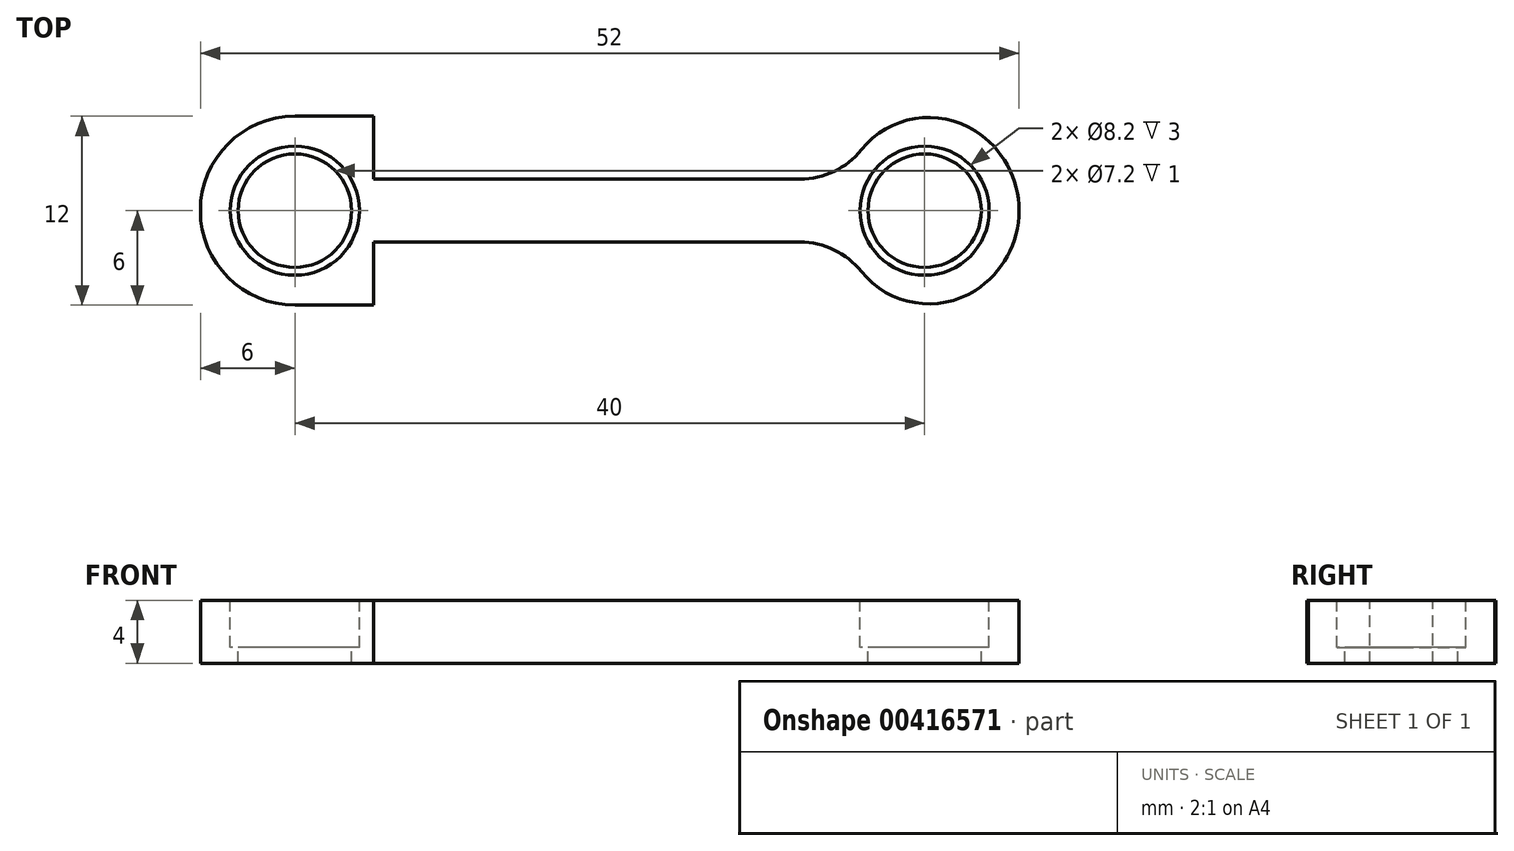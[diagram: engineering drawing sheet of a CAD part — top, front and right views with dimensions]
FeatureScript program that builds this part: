
annotation { "Feature Type Name" : "Feature", "Feature Type Description" : "" }
export const myFeature = defineFeature(function(context is Context, id is Id, definition is map)
    precondition{}
    {
        {
            var Q0;
            Q0=qCreatedBy(makeId("Top.planeOp"),FACE);
            var sketch = newSketch(context, id + "F0", { "sketchPlane" : qUnion([Q0])});
            skLineSegment(sketch, "E0.bottom", {"start": v(-19.88, 0) * mm, "end": v(32.12, 0) * mm});
            skLineSegment(sketch, "E0.top", {"start": v(-19.88, 12) * mm, "end": v(32.12, 12) * mm});
            skLineSegment(sketch, "E0.left", {"start": v(-19.88, 0) * mm, "end": v(-19.88, 12) * mm});
            skLineSegment(sketch, "E0.right", {"start": v(32.12, 0) * mm, "end": v(32.12, 12) * mm});
            skSolve(sketch);
        }
        {
            var Q0;
            Q0=makeQuery(id+"F0.imprint","IMPRINT",FACE,{"disambiguationData":[TD([[makeQuery(id+"F0.imprint","IMPRINT",EDGE,{"derivedFrom":sQuery(id+"F0.wireOp",EDGE,"E0.bottom")}),1.0]])]});
            extrude(context, id + "F1", {"entities" : qUnion([Q0]), "depth" : 4 * mm});
        }
        {
            var Q0;
            Q0=makeQuery(id+"F1.opExtrude","CAP_FACE",FACE,{"disambiguationData":[OSD([sQuery(id+"F0.wireOp",EDGE,"E0.bottom"),sQuery(id+"F0.wireOp",EDGE,"E0.top"),sQuery(id+"F0.wireOp",EDGE,"E0.left"),sQuery(id+"F0.wireOp",EDGE,"E0.right")])],"isStart":false});
            var sketch = newSketch(context, id + "F2", { "sketchPlane" : qUnion([Q0])});
            skCircle(sketch, "E1", {"center": v(26.12, 6) * mm, "radius": 4.1 * mm});
            skCircle(sketch, "E2", {"center": v(-13.88, 6) * mm, "radius": 4.1 * mm});
            skCircle(sketch, "E3", {"center": v(26.12, 6) * mm, "radius": 3.6 * mm});
            skCircle(sketch, "E4", {"center": v(-13.88, 6) * mm, "radius": 3.6 * mm});
            skSolve(sketch);
        }
        {
            var Q0;
            Q0=makeQuery(id+"F2.imprint","IMPRINT",FACE,{"disambiguationData":[TD([[makeQuery(id+"F2.imprint","IMPRINT",EDGE,{"derivedFrom":sQuery(id+"F2.wireOp",EDGE,"E2")}),1.0]])]});
            var Q1;
            Q1=makeQuery(id+"F2.imprint","IMPRINT",FACE,{"disambiguationData":[TD([[makeQuery(id+"F2.imprint","IMPRINT",EDGE,{"derivedFrom":sQuery(id+"F2.wireOp",EDGE,"KRTfRChP-nXbi-TgXD-2Nc6-GMDFCuTp6KQj")}),1.0]])]});
            var Q2;
            Q2=makeQuery(id+"F2.imprint","IMPRINT",FACE,{"disambiguationData":[TD([[makeQuery(id+"F2.imprint","IMPRINT",EDGE,{"derivedFrom":sQuery(id+"F2.wireOp",EDGE,"E1")}),1.0]])]});
            extrude(context, id + "F3", {"entities" : qUnion([Q0, Q1, Q2]), "operationType" : NewBodyOperationType.REMOVE, "oppositeDirection" : true, "depth" : 3 * mm});
        }
        {
            var Q0;
            Q0=makeQuery(id+"F2.imprint","IMPRINT",FACE,{"disambiguationData":[TD([[makeQuery(id+"F2.imprint","IMPRINT",EDGE,{"derivedFrom":sQuery(id+"F2.wireOp",EDGE,"E4")}),1.0]])]});
            var Q1;
            Q1=makeQuery(id+"F2.imprint","IMPRINT",FACE,{"disambiguationData":[TD([[makeQuery(id+"F2.imprint","IMPRINT",EDGE,{"derivedFrom":sQuery(id+"F2.wireOp",EDGE,"GlQmYsD8-ChJU-Foso-C0s5-5TPi7Piaeb3v")}),1.0]])]});
            var Q2;
            Q2=makeQuery(id+"F2.imprint","IMPRINT",FACE,{"disambiguationData":[TD([[makeQuery(id+"F2.imprint","IMPRINT",EDGE,{"derivedFrom":sQuery(id+"F2.wireOp",EDGE,"E3")}),1.0]])]});
            extrude(context, id + "F4", {"entities" : qUnion([Q0, Q1, Q2]), "operationType" : NewBodyOperationType.REMOVE, "oppositeDirection" : true, "depth" : 25 * mm});
        }
        {
            var Q0;
            Q0=makeQuery(id+"F1.opExtrude","SWEPT_EDGE",EDGE,{"disambiguationData":[OSD([sQuery(id+"F0.wireOp",EDGE,"E0.top"),sQuery(id+"F0.wireOp",EDGE,"E0.right")])]});
            var Q1;
            Q1=makeQuery(id+"F1.opExtrude","SWEPT_EDGE",EDGE,{"disambiguationData":[OSD([sQuery(id+"F0.wireOp",EDGE,"E0.bottom"),sQuery(id+"F0.wireOp",EDGE,"E0.right")])]});
            var Q2;
            Q2=makeQuery(id+"F1.opExtrude","SWEPT_EDGE",EDGE,{"disambiguationData":[OSD([sQuery(id+"F0.wireOp",EDGE,"E0.top"),sQuery(id+"F0.wireOp",EDGE,"E0.left")])]});
            var Q3;
            Q3=makeQuery(id+"F1.opExtrude","SWEPT_EDGE",EDGE,{"disambiguationData":[OSD([sQuery(id+"F0.wireOp",EDGE,"E0.bottom"),sQuery(id+"F0.wireOp",EDGE,"E0.left")])]});
            fillet(context, id + "F5", {"entities" : qUnion([Q0, Q1, Q2, Q3]), "radius" : 6 * mm, "tangentPropagation" : true, "allowEdgeOverflow" : false});
        }
        {
            var Q0;
            Q0=makeQuery(id+"F2.imprint","IMPRINT",FACE,{"disambiguationData":[TD([[makeQuery(id+"F2.imprint","IMPRINT",EDGE,{"derivedFrom":sQuery(id+"F2.wireOp",EDGE,"E1")}),-1.0]])]});
            var sketch = newSketch(context, id + "F6", { "sketchPlane" : qUnion([Q0])});
            skLineSegment(sketch, "E5.bottom", {"start": v(-8.88, 12) * mm, "end": v(21.12, 12) * mm});
            skLineSegment(sketch, "E5.top", {"start": v(-8.88, 8) * mm, "end": v(21.12, 8) * mm});
            skLineSegment(sketch, "E5.left", {"start": v(-8.88, 12) * mm, "end": v(-8.88, 8) * mm});
            skLineSegment(sketch, "E5.right", {"start": v(21.12, 12) * mm, "end": v(21.12, 8) * mm});
            skLineSegment(sketch, "E6.bottom", {"start": v(-8.88, 0) * mm, "end": v(21.12, 0) * mm});
            skLineSegment(sketch, "E6.top", {"start": v(-8.88, 4) * mm, "end": v(21.12, 4) * mm});
            skLineSegment(sketch, "E6.left", {"start": v(-8.88, 0) * mm, "end": v(-8.88, 4) * mm});
            skLineSegment(sketch, "E6.right", {"start": v(21.12, 0) * mm, "end": v(21.12, 4) * mm});
            skSolve(sketch);
        }
        {
            var Q0;
            Q0=makeQuery(id+"F6.imprint","IMPRINT",FACE,{"disambiguationData":[TD([[makeQuery(id+"F6.imprint","IMPRINT",EDGE,{"derivedFrom":sQuery(id+"F6.wireOp",EDGE,"E5.bottom")}),-1.0]])]});
            var Q1;
            Q1=makeQuery(id+"F6.imprint","IMPRINT",FACE,{"disambiguationData":[TD([[makeQuery(id+"F6.imprint","IMPRINT",EDGE,{"derivedFrom":sQuery(id+"F6.wireOp",EDGE,"E6.bottom")}),1.0]])]});
            extrude(context, id + "F7", {"entities" : qUnion([Q0, Q1]), "operationType" : NewBodyOperationType.REMOVE, "oppositeDirection" : true, "depth" : 25 * mm});
        }
        {
            var Q0;
            Q0=makeQuery(id+"F7.boolean.opBoolean","COPY",EDGE,{"derivedFrom":makeQuery(id+"F7.opExtrude","SWEPT_EDGE",EDGE,{"disambiguationData":[OSD([sQuery(id+"F0.wireOp",EDGE,"E0.top"),sQuery(id+"F6.wireOp",EDGE,"E5.bottom"),sQuery(id+"F6.wireOp",EDGE,"E5.left")])]})});
            var Q1;
            Q1=makeQuery(id+"F7.boolean.opBoolean","COPY",EDGE,{"derivedFrom":makeQuery(id+"F7.opExtrude","SWEPT_EDGE",EDGE,{"disambiguationData":[OSD([sQuery(id+"F0.wireOp",EDGE,"E0.bottom"),sQuery(id+"F6.wireOp",EDGE,"E6.bottom"),sQuery(id+"F6.wireOp",EDGE,"E6.left")])]})});
            var Q2;
            Q2=makeQuery(id+"F7.boolean.opBoolean","COPY",EDGE,{"derivedFrom":makeQuery(id+"F7.opExtrude","SWEPT_EDGE",EDGE,{"disambiguationData":[OSD([sQuery(id+"F0.wireOp",EDGE,"E0.bottom"),sQuery(id+"F6.wireOp",EDGE,"E6.bottom"),sQuery(id+"F6.wireOp",EDGE,"E6.right")])]})});
            var Q3;
            Q3=makeQuery(id+"F7.boolean.opBoolean","COPY",EDGE,{"derivedFrom":makeQuery(id+"F7.opExtrude","SWEPT_EDGE",EDGE,{"disambiguationData":[OSD([sQuery(id+"F0.wireOp",EDGE,"E0.top"),sQuery(id+"F6.wireOp",EDGE,"E5.bottom"),sQuery(id+"F6.wireOp",EDGE,"E5.right")])]})});
            fillet(context, id + "F8", {"entities" : qUnion([Q0, Q1, Q2, Q3]), "radius" : 5.5 * mm, "tangentPropagation" : true, "allowEdgeOverflow" : false});
        }
        {
            var Q0;
            Q0=makeQuery(id+"F8.opFillet","BLEND_EDGE",EDGE,{"blendedFrom":[makeQuery(id+"F7.boolean.opBoolean","COPY",EDGE,{"derivedFrom":makeQuery(id+"F7.opExtrude","SWEPT_EDGE",EDGE,{"disambiguationData":[OSD([sQuery(id+"F0.wireOp",EDGE,"E0.top"),sQuery(id+"F6.wireOp",EDGE,"E5.bottom"),sQuery(id+"F6.wireOp",EDGE,"E5.left")])]})}),makeQuery(id+"F7.boolean.opBoolean","COPY",FACE,{"derivedFrom":makeQuery(id+"F7.opExtrude","SWEPT_FACE",FACE,{"disambiguationData":[OSD([sQuery(id+"F6.wireOp",EDGE,"E5.top")])]})})],"blendedInto":[makeQuery(id+"F7.boolean.opBoolean","COPY",FACE,{"derivedFrom":makeQuery(id+"F7.opExtrude","SWEPT_FACE",FACE,{"disambiguationData":[OSD([sQuery(id+"F6.wireOp",EDGE,"E5.top")])]})})]});
            var Q1;
            Q1=makeQuery(id+"F8.opFillet","BLEND_EDGE",EDGE,{"blendedFrom":[makeQuery(id+"F7.boolean.opBoolean","COPY",EDGE,{"derivedFrom":makeQuery(id+"F7.opExtrude","SWEPT_EDGE",EDGE,{"disambiguationData":[OSD([sQuery(id+"F0.wireOp",EDGE,"E0.bottom"),sQuery(id+"F6.wireOp",EDGE,"E6.bottom"),sQuery(id+"F6.wireOp",EDGE,"E6.left")])]})}),makeQuery(id+"F7.boolean.opBoolean","COPY",FACE,{"derivedFrom":makeQuery(id+"F7.opExtrude","SWEPT_FACE",FACE,{"disambiguationData":[OSD([sQuery(id+"F6.wireOp",EDGE,"E6.top")])]})})],"blendedInto":[makeQuery(id+"F7.boolean.opBoolean","COPY",FACE,{"derivedFrom":makeQuery(id+"F7.opExtrude","SWEPT_FACE",FACE,{"disambiguationData":[OSD([sQuery(id+"F6.wireOp",EDGE,"E6.top")])]})})]});
            var Q2;
            Q2=makeQuery(id+"F8.opFillet","BLEND_EDGE",EDGE,{"blendedFrom":[makeQuery(id+"F7.boolean.opBoolean","COPY",EDGE,{"derivedFrom":makeQuery(id+"F7.opExtrude","SWEPT_EDGE",EDGE,{"disambiguationData":[OSD([sQuery(id+"F0.wireOp",EDGE,"E0.top"),sQuery(id+"F6.wireOp",EDGE,"E5.bottom"),sQuery(id+"F6.wireOp",EDGE,"E5.right")])]})}),makeQuery(id+"F7.boolean.opBoolean","COPY",FACE,{"derivedFrom":makeQuery(id+"F7.opExtrude","SWEPT_FACE",FACE,{"disambiguationData":[OSD([sQuery(id+"F6.wireOp",EDGE,"E5.top")])]})})],"blendedInto":[makeQuery(id+"F7.boolean.opBoolean","COPY",FACE,{"derivedFrom":makeQuery(id+"F7.opExtrude","SWEPT_FACE",FACE,{"disambiguationData":[OSD([sQuery(id+"F6.wireOp",EDGE,"E5.top")])]})})]});
            var Q3;
            Q3=makeQuery(id+"F8.opFillet","BLEND_EDGE",EDGE,{"blendedFrom":[makeQuery(id+"F7.boolean.opBoolean","COPY",EDGE,{"derivedFrom":makeQuery(id+"F7.opExtrude","SWEPT_EDGE",EDGE,{"disambiguationData":[OSD([sQuery(id+"F0.wireOp",EDGE,"E0.bottom"),sQuery(id+"F6.wireOp",EDGE,"E6.bottom"),sQuery(id+"F6.wireOp",EDGE,"E6.right")])]})}),makeQuery(id+"F7.boolean.opBoolean","COPY",FACE,{"derivedFrom":makeQuery(id+"F7.opExtrude","SWEPT_FACE",FACE,{"disambiguationData":[OSD([sQuery(id+"F6.wireOp",EDGE,"E6.top")])]})})],"blendedInto":[makeQuery(id+"F7.boolean.opBoolean","COPY",FACE,{"derivedFrom":makeQuery(id+"F7.opExtrude","SWEPT_FACE",FACE,{"disambiguationData":[OSD([sQuery(id+"F6.wireOp",EDGE,"E6.top")])]})})]});
            fillet(context, id + "F9", {"entities" : qUnion([Q0, Q1, Q2, Q3]), "radius" : 5 * mm, "tangentPropagation" : true, "allowEdgeOverflow" : false});
        }
    });
